# Revit family: P200598WL-001c_WFW5090J
name_source: partatom
category: Specialty Equipment
units: mm (PartAtom-declared; Revit-internal decimal feet)

## family parameters
Always vertical = Yes
Cut with Voids When Loaded = No
Enable Cutting in Views = No
Maintain Annotation Orientation = No
Part Type = Normal
Room Calculation Point = No
Round Connector Dimension = Use Diameter
Shared = No
Work Plane-Based = No

## types (1)
- WFW5090JW
    Amps = 0 A
    Back Panel Material = ARCAT - Metal - Aluminum
    Body Material = ARCAT - Plastic - White
    Chrome Trim Material = ARCAT - Metal - Chrome
    Clearance Material = ARCAT - Clearance
    Default Elevation = 0"
    Depth = 25 1/8"
    Description = 2.3 cu. ft. 24" Compact Washer with Detergent Dosing Aid option
Laveuse compacte de 24 po, 2,3 pi³ avec option d’aide-doseur de détergent
    Dimension Guide = http://access.whirlpool.com Guide&sku=WFW5090JW&language=EN
http://access.whirlpool.com Guide&sku=WFW5090JW&language=EN
    Display Panel Material = ARCAT - Glass Tempered - Black
    Door Material = ARCAT - Plastic - White
    Energy Guide = https://www.whirlpool.com
https://www.whirlpool.com
    Family Name = Compact Washer
    Feature 1 = Space-saving design at 2.3 cu. ft.
Space-saving design at 2.3 cu. ft.
    Feature 2 = Detergent Dosing Aid
Aide-doseur de détergent
    Feature 3 = Save Time option
Sanitize option
Option d'assainissement
    Glass Material = ARCAT - Glass Tempered - Clear
    Height = 33 1/4"
    Installation-Fabrication = http://access.whirlpool.com Instruction&sku=WFW5090JW&language=EN
http://access.whirlpool.com Instruction&sku=WFW5090JW&language=EN
    Knob Material = ARCAT - Plastic - Gray
    Manufacturer = Whirlpool
    Model = WFW5090JW
    Voltage = 0 V
    Width = 24"

## geometry (parser evidence)
native form markers: Sweep x3
no freeform markers — native parametric forms only
